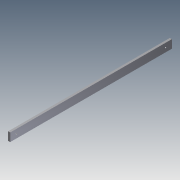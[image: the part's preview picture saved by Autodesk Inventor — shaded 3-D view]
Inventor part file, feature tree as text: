
AUTODESK INVENTOR PART (.ipt)
format: ipt  version: 2011 (Build 150239000, 239)  size: 84,480 bytes
history: native  units: in
note: dims shown in document units (in); Inventor stores cm internally (conversion verified against a paired STEP export)
features: extrude x2, sketch x2
ambient origin geometry x8: Origin, YZ Plane, XZ Plane, XY Plane, X Axis, Y Axis, Z Axis, Center Point
bodies: Solid1 (feature_tree)
feature tree (4):
  extrude  "Extrusion1"  Depth=1.0in
  extrude  "Extrusion2"  Depth=1.25in
  sketch  "Sketch1"  dims[d0=0.25in d1=1.0in]
  sketch  "Sketch2"  dims[d2=19.5in d3=0.0in d4=1.25in d5=0.25in d6=0.156in d7=1.25in d8=45.0deg d9=1.0in d10=0.0in]
